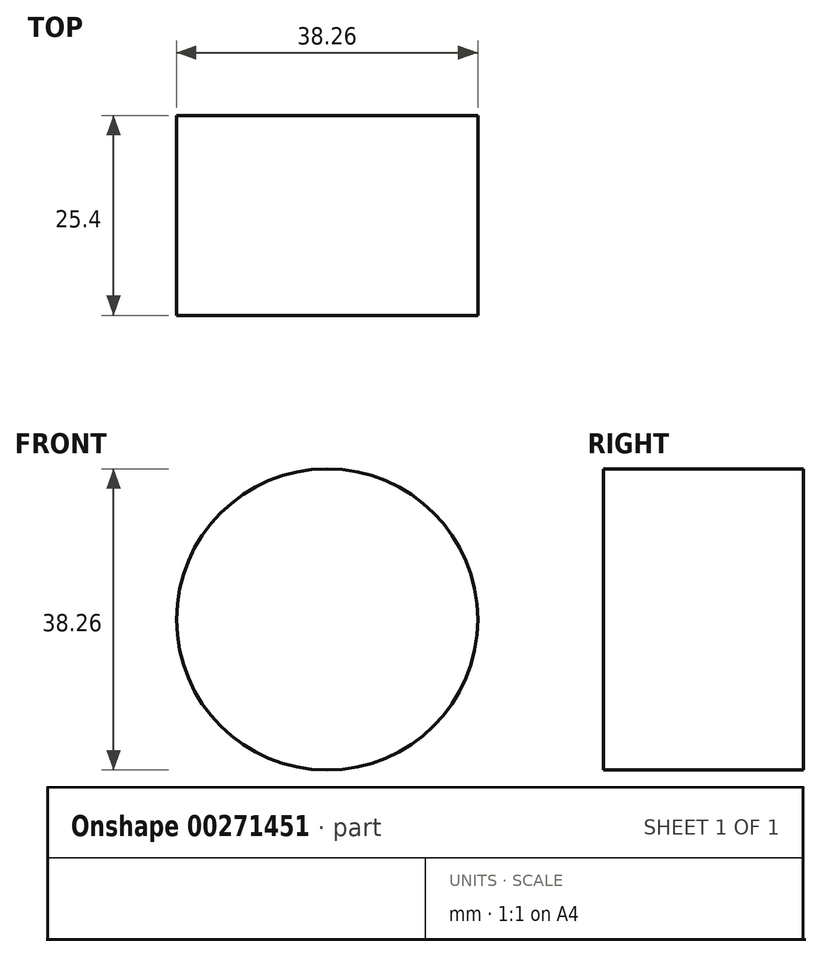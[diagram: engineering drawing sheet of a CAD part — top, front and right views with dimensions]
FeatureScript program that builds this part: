
annotation { "Feature Type Name" : "Feature", "Feature Type Description" : "" }
export const myFeature = defineFeature(function(context is Context, id is Id, definition is map)
    precondition{}
    {
        {
            var Q0;
            Q0=qCreatedBy(makeId("Front.planeOp"),FACE);
            var sketch = newSketch(context, id + "F0", { "sketchPlane" : qUnion([Q0])});
            skCircle(sketch, "E0", {"center": v(0, 0) * mm, "radius": 19.13 * mm});
            skSolve(sketch);
        }
        {
            var Q0;
            Q0=makeQuery(id+"F0.imprint","IMPRINT",FACE,{"disambiguationData":[TD([[makeQuery(id+"F0.imprint","IMPRINT",EDGE,{"derivedFrom":sQuery(id+"F0.wireOp",EDGE,"E0")}),1.0]])]});
            extrude(context, id + "F1", {"entities" : qUnion([Q0]), "depth" : 25.4 * mm});
        }
    });
